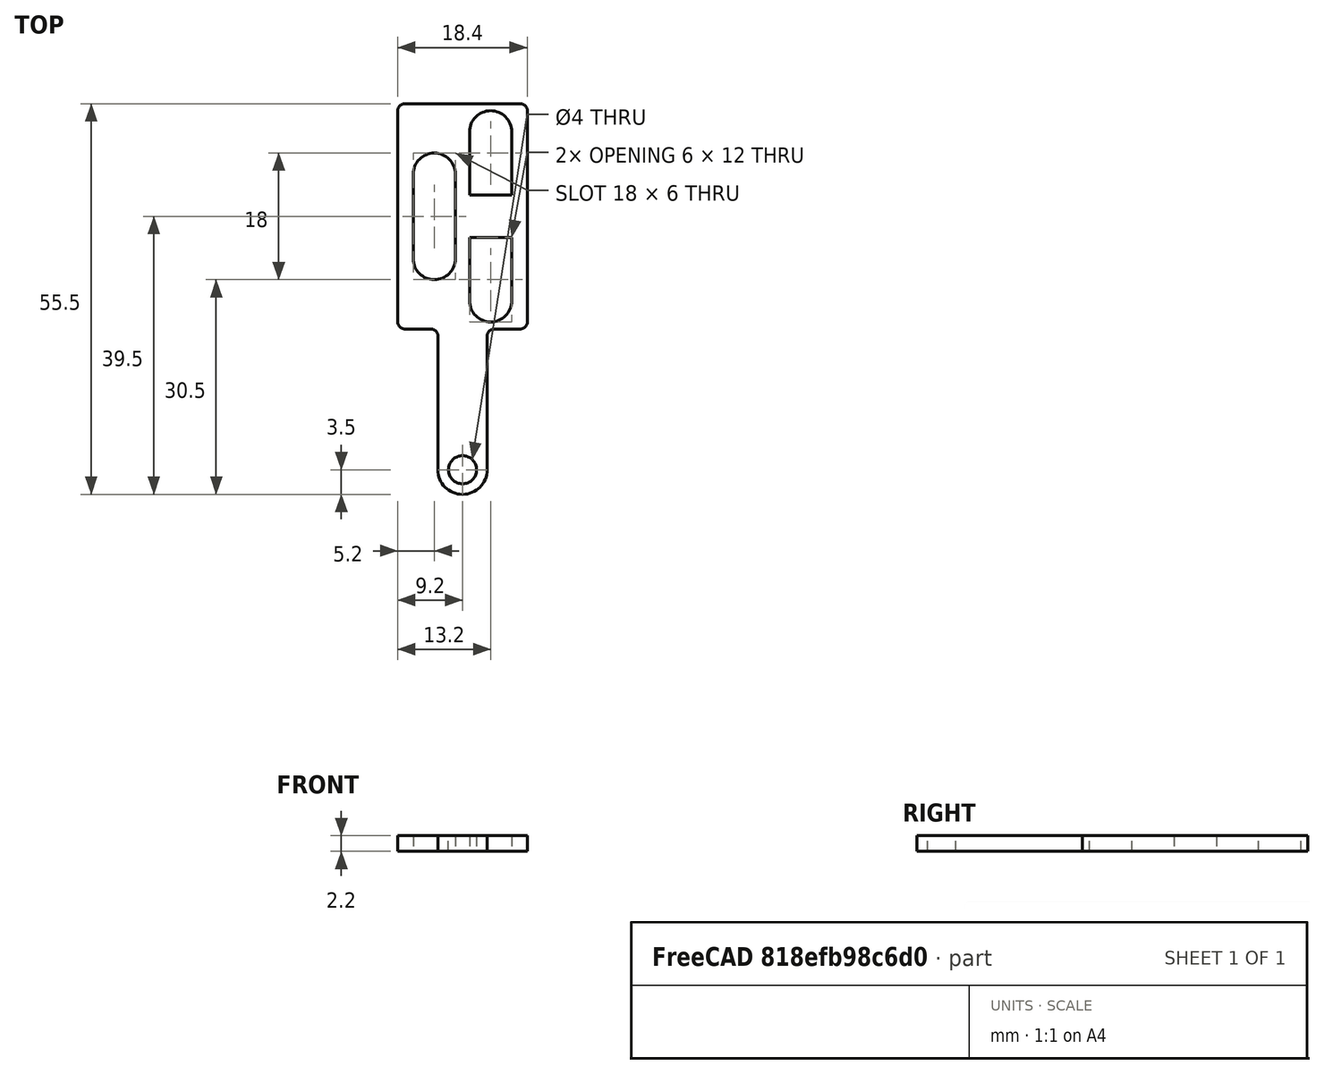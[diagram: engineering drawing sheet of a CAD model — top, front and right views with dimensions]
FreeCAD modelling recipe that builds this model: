
FCSTD DOCUMENT  (FreeCAD 0.18R16131 (Git))
Label: VALVE.STI (1)
License: All rights reserved
LicenseURL: http://en.wikipedia.org/wiki/All_rights_reserved
objects: TechDraw::DrawViewDimension×12, TechDraw::DrawProjGroupItem×4, Sketcher::SketchObject×2, TechDraw::DrawSVGTemplate×2, TechDraw::DrawPage×2, PartDesign::Pad×1, PartDesign::Fillet×1, PartDesign::Plane×1, PartDesign::Pocket×1, PartDesign::Body×1, TechDraw::DrawViewPart×1, TechDraw::DrawProjGroup×1
note: 9 computed .brp shape members not serialized (recipe doc carries the construction recipe); baked Part::Feature solids carry a one-line shape summary decoded from their .brp

FEATURE [Sketcher::SketchObject] Sketch
  MapMode = 5
  Support = -> [XY_Plane]
  sketch-geometry (12):
    g0: LineSegment StartX=-9.2 StartY=16 StartZ=0 EndX=9.2 EndY=16 EndZ=0
    g1: LineSegment StartX=9.2 StartY=16 StartZ=0 EndX=9.2 EndY=-16 EndZ=0
    g2: LineSegment StartX=9.2 StartY=-16 StartZ=0 EndX=4.5 EndY=-16 EndZ=0
    g3: LineSegment StartX=4.5 StartY=-16 StartZ=0 EndX=4.5 EndY=-17 EndZ=0
    g4: LineSegment StartX=4.5 StartY=-17 StartZ=0 EndX=3.5 EndY=-17 EndZ=0
    g5: LineSegment StartX=3.5 StartY=-17 StartZ=0 EndX=3.5 EndY=-36 EndZ=0
    g6: LineSegment StartX=-3.5 StartY=-36 StartZ=0 EndX=-3.5 EndY=-17 EndZ=0
    g7: LineSegment StartX=-3.5 StartY=-17 StartZ=0 EndX=-4.5 EndY=-17 EndZ=0
    g8: LineSegment StartX=-4.5 StartY=-17 StartZ=0 EndX=-4.5 EndY=-16 EndZ=0
    g9: LineSegment StartX=-4.5 StartY=-16 StartZ=0 EndX=-9.2 EndY=-16 EndZ=0
    g10: LineSegment StartX=-9.2 StartY=-16 StartZ=0 EndX=-9.2 EndY=16 EndZ=0
    g11: ArcOfCircle CenterX=0 CenterY=-36 CenterZ=0 NormalX=0 NormalY=0 NormalZ=1 AngleXU=0 Radius=3.5 StartAngle=3.14159 EndAngle=6.28319
  constraints (35):
    c: Coincident(g0,g1)
    c: Coincident(g1,g2)
    c: Horizontal(g2)
    c: Coincident(g2,g3)
    c: Coincident(g3,g4)
    c: Coincident(g4,g5)
    c: Vertical(g6)
    c: Coincident(g6,g7)
    c: Coincident(g7,g8)
    c: Coincident(g8,g9)
    c: Coincident(g9,g10)
    c: Vertical(g10)
    c: Coincident(g0,g10)
    c: Horizontal(g9)
    c: Horizontal(g4)
    c: Horizontal(g7)
    c: Vertical(g3)
    c: Vertical(g5)
    c: Vertical(g8)
    c: Distance(g0) = 18.4
    c: Distance(g2) = 4.7
    c: Distance(g4) = 1
    c: Distance(g7) = 1
    c: Distance(g8) = 1
    c: Distance(g3) = 1
    c: Distance(g6) = 19
    c: Distance(g5) = 19
    c: Distance(g1) = 32
    c: Radius(g11) = 3.5
    c: Coincident(g11,g5)
    c: Coincident(g11,g6)
    c: Distance(g10) = 32
    c: Symmetric(g0,g0,g-2)
    c: Symmetric(g1,g0,g-1)
    c: Distance(g9) = 4.7
FEATURE [PartDesign::Pad] Pad
  Length = 2.2
  Length2 = 100
  Profile = -> Sketch
  Type = 0
FEATURE [PartDesign::Fillet] Fillet
  Base = -> Pad [Edge14,Edge17,Edge20,Edge11]
  BaseFeature = -> Pad
  Radius = 1
FEATURE [PartDesign::Plane] DatumPlane
  Length = 26.6618
  MapMode = 5
  Placement = pos=(0,0,2.2) rot=(0,0,1;0rad)
  ResizeMode = 0
  Support = -> [Fillet]
  Width = 62.1363
FEATURE [Sketcher::SketchObject] Sketch001
  ExternalGeometry = -> [Fillet]
  MapMode = 5
  Placement = pos=(0,0,2.2) rot=(0,0,1;0rad)
  Support = -> [DatumPlane]
  sketch-geometry (15):
    g0: ArcOfCircle CenterX=-4 CenterY=6 CenterZ=0 NormalX=0 NormalY=0 NormalZ=1 AngleXU=0 Radius=3 StartAngle=2.93e-06 EndAngle=3.14159
    g1: ArcOfCircle CenterX=-4 CenterY=-6 CenterZ=0 NormalX=0 NormalY=0 NormalZ=1 AngleXU=0 Radius=3 StartAngle=3.14159 EndAngle=6.28319
    g2: LineSegment StartX=-7 StartY=-6 StartZ=0 EndX=-7 EndY=6 EndZ=0
    g3: LineSegment StartX=-1 StartY=-5.99999 StartZ=0 EndX=-1 EndY=6.00001 EndZ=0
    g4: LineSegment StartX=1 StartY=12 StartZ=0 EndX=1 EndY=3 EndZ=0
    g5: LineSegment StartX=1 StartY=3 StartZ=0 EndX=7 EndY=3 EndZ=0
    g6: LineSegment StartX=7 StartY=3 StartZ=0 EndX=7 EndY=12 EndZ=0
    g7: LineSegment StartX=1 StartY=-12 StartZ=0 EndX=1 EndY=-3 EndZ=0
    g8: LineSegment StartX=1 StartY=-3 StartZ=0 EndX=7 EndY=-3 EndZ=0
    g9: LineSegment StartX=7 StartY=-3 StartZ=0 EndX=7 EndY=-12 EndZ=0
    g10: ArcOfCircle CenterX=4 CenterY=12 CenterZ=0 NormalX=0 NormalY=0 NormalZ=1 AngleXU=0 Radius=3 StartAngle=6.22048e-09 EndAngle=3.14159
    g11: ArcOfCircle CenterX=4 CenterY=-12 CenterZ=0 NormalX=0 NormalY=0 NormalZ=1 AngleXU=0 Radius=3 StartAngle=3.14159 EndAngle=6.28319
    g12: Circle CenterX=0 CenterY=-36 CenterZ=0 NormalX=0 NormalY=0 NormalZ=1 AngleXU=0 Radius=2
    g13: Circle CenterX=-4.5 CenterY=-17 CenterZ=0 NormalX=0 NormalY=0 NormalZ=1 AngleXU=0 Radius=1
    g14: Circle CenterX=4.5 CenterY=-17 CenterZ=0 NormalX=0 NormalY=0 NormalZ=1 AngleXU=0 Radius=1
  constraints (46):
    c: Coincident(g2,g1)
    c: Coincident(g2,g0)
    c: Coincident(g3,g1)
    c: Coincident(g3,g0)
    c: Vertical(g3)
    c: Vertical(g2)
    c: Radius(g0) = 3
    c: Radius(g1) = 3
    c: DistanceY(g2,g2) = 12
    c: DistanceY(g3,g3) = 12
    c: DistanceX(g1,g1) = 6
    c: DistanceX(g-3,g0) = 2.2
    c: DistanceY(g0,g-4) = 10
    c: Vertical(g4)
    c: Coincident(g4,g5)
    c: Horizontal(g5)
    c: Coincident(g5,g6)
    c: Vertical(g7)
    c: Coincident(g7,g8)
    c: Coincident(g8,g9)
    c: Vertical(g9)
    c: Vertical(g6)
    c: Horizontal(g8)
    c: Coincident(g11,g7)
    c: Coincident(g9,g11)
    c: Coincident(g10,g6)
    c: Coincident(g10,g4)
    c: Radius(g10) = 3
    c: Radius(g11) = 3
    c: Distance(g4) = 9
    c: Distance(g6) = 9
    c: Distance(g9) = 9
    c: Distance(g7) = 9
    c: Distance(g8) = 6
    c: Distance(g5) = 6
    c: DistanceY(g7,g4) = 6
    c: DistanceX(g4,g7) = 0
    c: DistanceY(g5,g-4) = 13
    c: DistanceX(g0,g4) = 2
    c: PointOnObject(g12,g-2)
    c: Radius(g12) = 2
    c: DistanceY(g12,g-5) = 0
    c: Radius(g13) = 1
    c: Radius(g14) = 1
    c: Coincident(g13,g-7)
    c: Coincident(g14,g-6)
FEATURE [PartDesign::Pocket] Pocket
  BaseFeature = -> Fillet
  Length = 5
  Length2 = 100
  Profile = -> Sketch001
  Type = 0
FEATURE [PartDesign::Body] Body
  Group = -> [Sketch,Pad,Fillet,DatumPlane,Sketch001,Pocket]
  Origin = -> Origin
  Tip = -> Pocket
FEATURE [TechDraw::DrawSVGTemplate] Template
  EditableTexts = Designed_by_Name=Designed by Name; Drawing_number=Drawing number; FC-Date=Date; FC-SC=Scale; FC-SH=Sheet; FC-Title=Title; Subtitle=Subtitle; Weight=Weight
  Height = 210
  Orientation = 1
  Width = 297
FEATURE [TechDraw::DrawViewPart] View
  CoarseView = false
  Direction = (1,0,0)
  Focus = 100
  HardHidden = false
  IsoCount = 0
  IsoHidden = false
  IsoVisible = false
  LockPosition = false
  Perspective = false
  Rotation = 0
  ScaleType = 0
  SeamHidden = false
  SeamVisible = false
  SmoothHidden = false
  SmoothVisible = false
  Source = -> [Body]
  X = 148.5
  Y = 105
FEATURE [TechDraw::DrawPage] Page
  KeepUpdated = true
  ProjectionType = 0
  Template = -> Template
  Views = -> [View]
FEATURE [TechDraw::DrawSVGTemplate] Template001
  EditableTexts = Approved1=Approved 1; Approved2=Approved 2; CheckedBy=Checked By; Code=Code; CompanyAddress=1234 Main St; CompanyName=Company Name; DrawingNumber=Drawing Number; DrawingTitle1=Drawing Title 1; DrawingTitle2=Drawing Title 2; DrawingTitle3=Drawing Title 3; DrawnBy=Drawn By; Revision=Rev; Scale=Scale; Sheet=Sheet n of m; Weight=Weight
  Height = 279.4
  Orientation = 1
  Width = 431.8
FEATURE [TechDraw::DrawProjGroupItem] ProjItem  label="Front"
  CoarseView = false
  Direction = (1,0,0)
  Focus = 100
  HardHidden = false
  IsoCount = 0
  IsoHidden = false
  IsoVisible = false
  LockPosition = true
  Perspective = false
  Rotation = 0
  RotationVector = (0,1,0)
  Scale = 2
  ScaleType = 2
  SeamHidden = false
  SeamVisible = false
  SmoothHidden = false
  SmoothVisible = false
  Source = -> [Body]
  Type = 0
  X = 0
  Y = 0
FEATURE [TechDraw::DrawProjGroupItem] ProjItem001  label="FrontTopLeft"
  CoarseView = false
  Direction = (1,-1,1)
  Focus = 100
  HardHidden = false
  IsoCount = 0
  IsoHidden = false
  IsoVisible = false
  LockPosition = false
  Perspective = false
  Rotation = 0
  RotationVector = (1,1,0)
  Scale = 2
  ScaleType = 2
  SeamHidden = false
  SeamVisible = false
  SmoothHidden = false
  SmoothVisible = false
  Source = -> [Body]
  Type = 6
  X = 126
  Y = -126
FEATURE [TechDraw::DrawProjGroupItem] ProjItem002  label="Left"
  CoarseView = false
  Direction = (1e-16,-1,0)
  Focus = 100
  HardHidden = false
  IsoCount = 0
  IsoHidden = false
  IsoVisible = false
  LockPosition = false
  Perspective = false
  Rotation = 0
  RotationVector = (1,1e-16,0)
  Scale = 2
  ScaleType = 2
  SeamHidden = false
  SeamVisible = false
  SmoothHidden = false
  SmoothVisible = false
  Source = -> [Body]
  Type = 1
  X = 126
  Y = 0
FEATURE [TechDraw::DrawProjGroupItem] ProjItem003  label="Top"
  CoarseView = false
  Direction = (0,0,1)
  Focus = 100
  HardHidden = false
  IsoCount = 0
  IsoHidden = false
  IsoVisible = false
  LockPosition = false
  Perspective = false
  Rotation = 0
  RotationVector = (0,1,0)
  Scale = 2
  ScaleType = 2
  SeamHidden = false
  SeamVisible = false
  SmoothHidden = false
  SmoothVisible = false
  Source = -> [Body]
  Type = 4
  X = 0
  Y = -126
FEATURE [TechDraw::DrawProjGroup] ProjGroup
  Anchor = -> ProjItem
  AutoDistribute = true
  LockPosition = false
  ProjectionType = 0
  Rotation = 0
  Scale = 2
  ScaleType = 2
  Source = -> [Body]
  Views = -> [ProjItem,ProjItem001,ProjItem002,ProjItem003]
  X = 88.6794
  Y = 234.335
  spacingX = 15
  spacingY = 15
FEATURE [TechDraw::DrawViewDimension] Dimension
  Arbitrary = false
  FormatSpec = %.2f
  LockPosition = false
  MeasureType = 1
  OverTolerance = 0
  References2D = -> [ProjItem002]
  Rotation = 0
  ScaleType = 0
  Type = 1
  UnderTolerance = 0
  X = -1.73325
  Y = -39.6382
FEATURE [TechDraw::DrawViewDimension] Dimension001
  Arbitrary = false
  FormatSpec = %.2f
  LockPosition = false
  MeasureType = 1
  OverTolerance = 0
  References2D = -> [ProjItem002]
  Rotation = 0
  ScaleType = 0
  Type = 1
  UnderTolerance = 0
  X = -3.4665
  Y = 18.8392
FEATURE [TechDraw::DrawViewDimension] Dimension002
  Arbitrary = false
  FormatSpec = %.2f
  LockPosition = false
  MeasureType = 1
  OverTolerance = 0
  References2D = -> [ProjItem002]
  Rotation = 0
  ScaleType = 0
  Type = 1
  UnderTolerance = 0
  X = -1.73325
  Y = -21.9591
FEATURE [TechDraw::DrawViewDimension] Dimension003
  Arbitrary = false
  FormatSpec = %.2f
  LockPosition = false
  MeasureType = 1
  OverTolerance = 0
  References2D = -> [ProjItem]
  Rotation = 0
  ScaleType = 0
  Type = 1
  UnderTolerance = 0
  X = -3.4665
  Y = -36.5184
FEATURE [TechDraw::DrawViewDimension] Dimension004
  Arbitrary = false
  FormatSpec = %.2f
  LockPosition = false
  MeasureType = 1
  OverTolerance = 0
  References2D = -> [ProjItem]
  Rotation = 0
  ScaleType = 0
  Type = 1
  UnderTolerance = 0
  X = 0.76677
  Y = 17.7993
FEATURE [TechDraw::DrawViewDimension] Dimension005
  Arbitrary = false
  FormatSpec = %.2f
  LockPosition = false
  MeasureType = 1
  OverTolerance = 0
  References2D = -> [ProjItem]
  Rotation = 0
  ScaleType = 0
  Type = 1
  UnderTolerance = 0
  X = 22.8067
  Y = -21.9591
FEATURE [TechDraw::DrawViewDimension] Dimension006
  Arbitrary = false
  FormatSpec = %.2f
  LockPosition = false
  MeasureType = 1
  OverTolerance = 0
  References2D = -> [ProjItem]
  Rotation = 0
  ScaleType = 0
  Type = 1
  UnderTolerance = 0
  X = -35.0464
  Y = -22.999
FEATURE [TechDraw::DrawViewDimension] Dimension007
  Arbitrary = false
  FormatSpec = %.2f
  LockPosition = false
  MeasureType = 1
  OverTolerance = 0
  References2D = -> [ProjItem003]
  Rotation = 0
  ScaleType = 0
  Type = 2
  UnderTolerance = 0
  X = 65.1792
  Y = -8.6933
FEATURE [TechDraw::DrawViewDimension] Dimension008
  Arbitrary = false
  FormatSpec = %.2f
  LockPosition = false
  MeasureType = 1
  OverTolerance = 0
  References2D = -> [ProjItem003]
  Rotation = 0
  ScaleType = 0
  Type = 2
  UnderTolerance = 0
  X = 61.8454
  Y = 27.0658
FEATURE [TechDraw::DrawViewDimension] Dimension009
  Arbitrary = false
  FormatSpec = %.2f
  LockPosition = false
  MeasureType = 1
  OverTolerance = 0
  References2D = -> [ProjItem003]
  Rotation = 0
  ScaleType = 0
  Type = 1
  UnderTolerance = 0
  X = 23.8467
  Y = 45.1985
FEATURE [TechDraw::DrawViewDimension] Dimension010
  Arbitrary = false
  FormatSpec = %.2f
  LockPosition = false
  MeasureType = 1
  OverTolerance = 0
  References2D = -> [ProjItem003]
  Rotation = 0
  ScaleType = 0
  Type = 1
  UnderTolerance = 0
  X = 8.50002
  Y = -39.3055
FEATURE [TechDraw::DrawViewDimension] Dimension011
  Arbitrary = false
  FormatSpec = %.2f
  LockPosition = false
  MeasureType = 1
  OverTolerance = 0
  References2D = -> [ProjItem003]
  Rotation = 0
  ScaleType = 0
  Type = 2
  UnderTolerance = 0
  X = -65.4858
  Y = 2.42655
FEATURE [TechDraw::DrawPage] Page001
  KeepUpdated = true
  ProjectionType = 0
  Template = -> Template001
  Views = -> [ProjGroup,Dimension,Dimension001,Dimension002,Dimension003,Dimension004,Dimension005,Dimension006,Dimension007,Dimension008,Dimension009,Dimension010,Dimension011]
